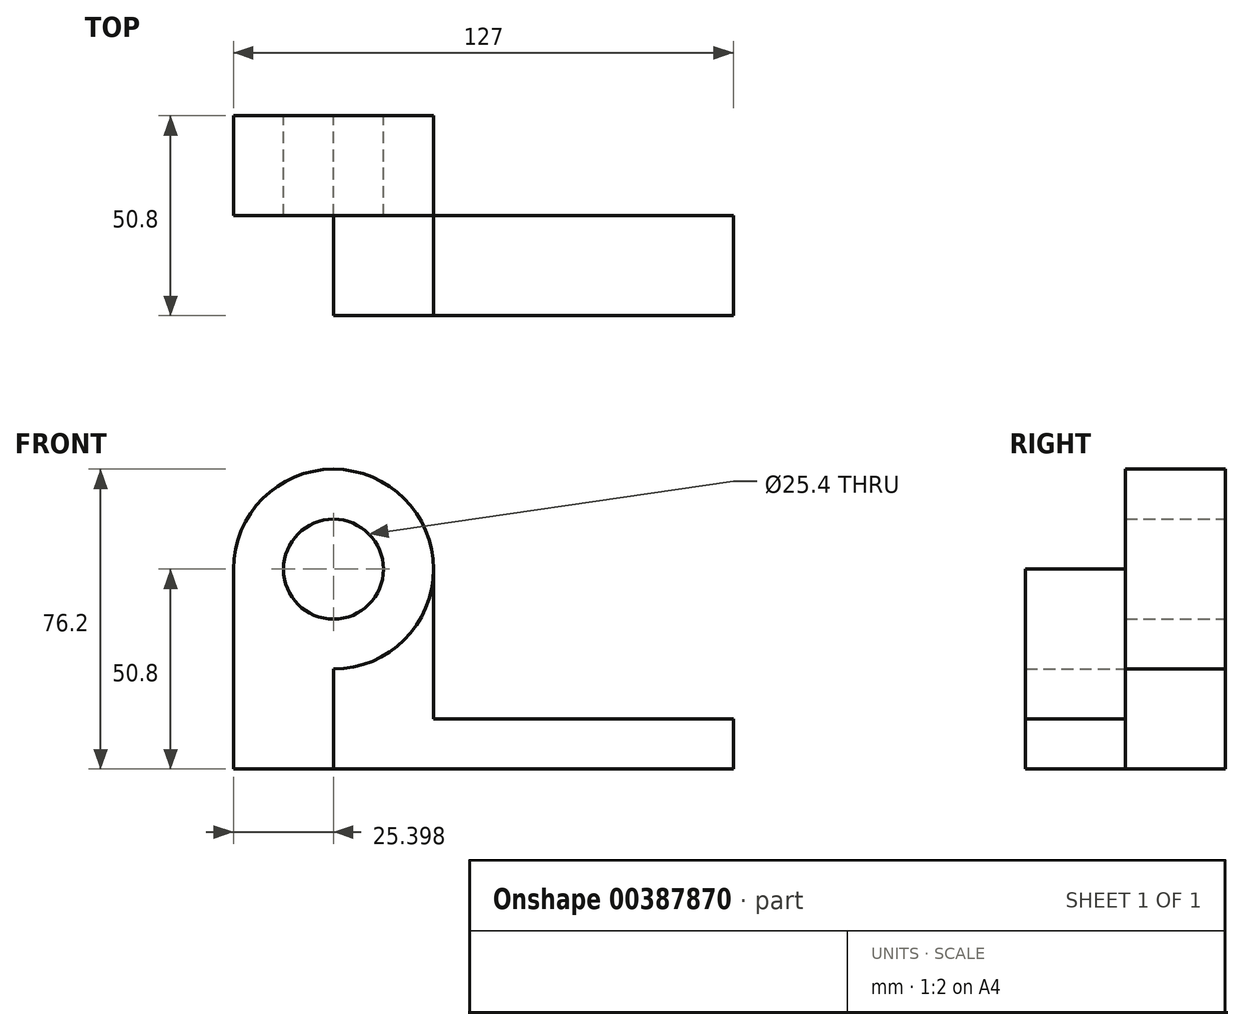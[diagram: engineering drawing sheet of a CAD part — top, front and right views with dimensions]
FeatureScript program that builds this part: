
annotation { "Feature Type Name" : "Feature", "Feature Type Description" : "" }
export const myFeature = defineFeature(function(context is Context, id is Id, definition is map)
    precondition{}
    {
        {
            var Q0;
            Q0=qCreatedBy(makeId("Front.planeOp"),FACE);
            var sketch = newSketch(context, id + "F0", { "sketchPlane" : qUnion([Q0])});
            skLineSegment(sketch, "E0", {"start": v(-76.67, -50.8) * mm, "end": v(50.33, -50.8) * mm});
            skLineSegment(sketch, "E1", {"start": v(-76.67, -50.8) * mm, "end": v(-76.67, 0) * mm});
            skLineSegment(sketch, "E2", {"start": v(50.33, -50.8) * mm, "end": v(50.33, -38.1) * mm});
            skLineSegment(sketch, "E3", {"start": v(-76.67, -50.8) * mm, "end": v(-51.27, -50.8) * mm});
            skLineSegment(sketch, "E4", {"start": v(-51.27, -50.8) * mm, "end": v(-51.27, 0) * mm});
            skCircle(sketch, "E5", {"center": v(-51.27, 0) * mm, "radius": 25.4 * mm});
            skCircle(sketch, "E6", {"center": v(-51.27, 0) * mm, "radius": 12.7 * mm});
            skLineSegment(sketch, "E7", {"start": v(50.33, -38.1) * mm, "end": v(-37.03, 21.03) * mm});
            skSolve(sketch);
        }
        {
            var Q0;
            Q0=makeQuery(id+"F0.imprint","IMPRINT",FACE,{"disambiguationData":[TD([[makeQuery(id+"F0.imprint","IMPRINT",EDGE,{"derivedFrom":sQuery(id+"F0.wireOp",EDGE,"E6")}),-1.0]])]});
            var Q1;
            {var subQ0=sQuery(id+"F0.wireOp",EDGE,"E1");Q1=makeQuery(id+"F0.imprint","IMPRINT",FACE,{"disambiguationData":[TD([[makeQuery(id+"F0.imprint","IMPRINT",EDGE,{"derivedFrom":subQ0}),-1.0]])]});}
            var Q2;
            {var subQ1=sQuery(id+"F0.wireOp",EDGE,"E0");Q2=makeQuery(id+"F0.imprint","IMPRINT",FACE,{"disambiguationData":[TD([[makeQuery(id+"F0.imprint","IMPRINT",EDGE,{"derivedFrom":subQ1}),1.0]])]});}
            extrude(context, id + "F1", {"entities" : qUnion([Q0, Q1, Q2]), "depth" : 25.4 * mm});
        }
        {
            var Q0;
            Q0=makeQuery(id+"F1.opExtrude","CAP_FACE",FACE,{"disambiguationData":[OSD([sQuery(id+"F0.wireOp",EDGE,"E0"),sQuery(id+"F0.wireOp",EDGE,"E1"),sQuery(id+"F0.wireOp",EDGE,"E2"),sQuery(id+"F0.wireOp",EDGE,"E3"),sQuery(id+"F0.wireOp",EDGE,"E5"),sQuery(id+"F0.wireOp",EDGE,"E6"),sQuery(id+"F0.wireOp",EDGE,"E7")])],"isStart":false});
            var sketch = newSketch(context, id + "F2", { "sketchPlane" : qUnion([Q0])});
            skLineSegment(sketch, "E8.bottom", {"start": v(50.33, -38.1) * mm, "end": v(-25.87, -38.1) * mm});
            skLineSegment(sketch, "E8.top", {"start": v(50.33, -50.8) * mm, "end": v(-76.67, -50.8) * mm});
            skLineSegment(sketch, "E8.left", {"start": v(50.33, -38.1) * mm, "end": v(50.33, -50.8) * mm});
            skLineSegment(sketch, "E8.right", {"start": v(-76.67, -38.1) * mm, "end": v(-76.67, -50.8) * mm});
            skCircle(sketch, "E9", {"center": v(-51.27, 0) * mm, "radius": 12.7 * mm});
            skArc(sketch, "E10", {"start": v(-25.87, 0) * mm, "mid": v(-51.27, 25.4) * mm, "end": v(-76.67, 0) * mm});
            skLineSegment(sketch, "E11", {"start": v(-76.67, 0) * mm, "end": v(-76.67, -38.1) * mm});
            skLineSegment(sketch, "E12", {"start": v(-25.87, 0) * mm, "end": v(-25.87, -38.1) * mm});
            skSolve(sketch);
        }
        {
            var Q0;
            Q0=makeQuery(id+"F2.imprint","IMPRINT",FACE,{"disambiguationData":[TD([[makeQuery(id+"F2.imprint","IMPRINT",EDGE,{"derivedFrom":sQuery(id+"F2.wireOp",EDGE,"E8.bottom")}),1.0]])]});
            extrude(context, id + "F3", {"entities" : qUnion([Q0]), "operationType" : NewBodyOperationType.ADD, "depth" : 25.4 * mm});
        }
    });
